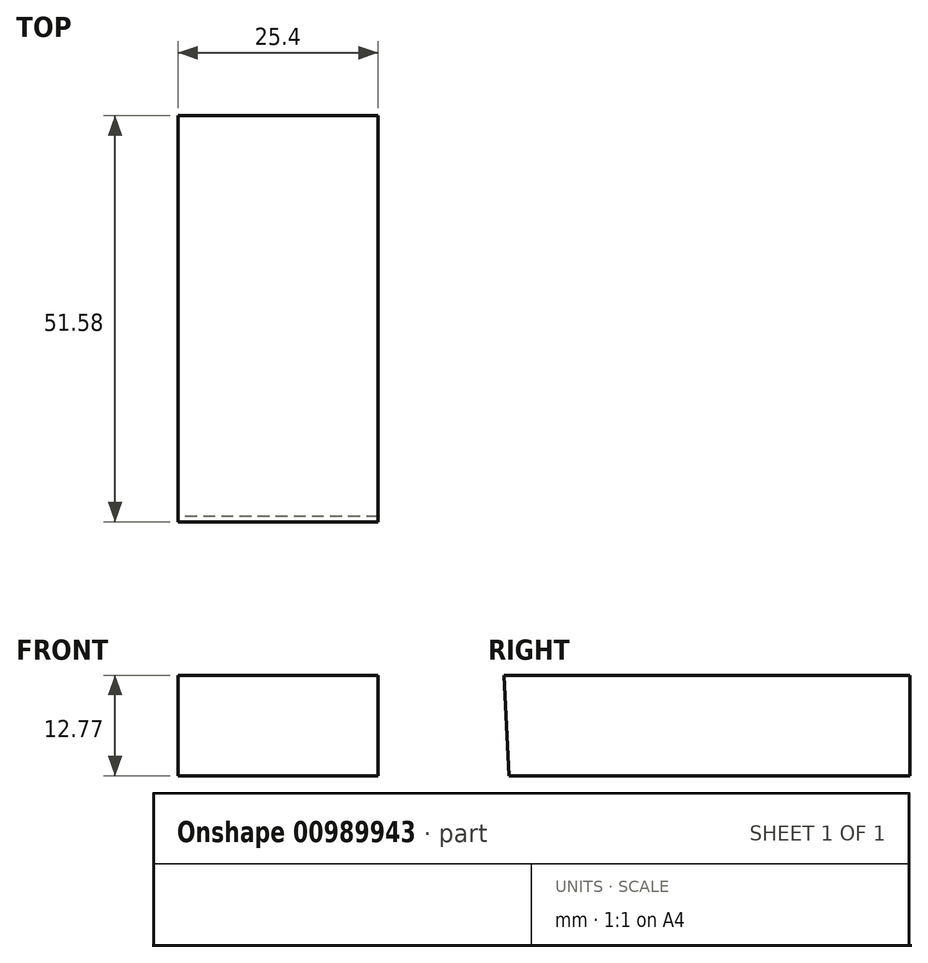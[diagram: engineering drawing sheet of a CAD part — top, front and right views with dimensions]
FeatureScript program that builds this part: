
annotation { "Feature Type Name" : "Feature", "Feature Type Description" : "" }
export const myFeature = defineFeature(function(context is Context, id is Id, definition is map)
    precondition{}
    {
        {
            var Q0;
            Q0=qCreatedBy(makeId("Right.planeOp"),FACE);
            var sketch = newSketch(context, id + "F0", { "sketchPlane" : qUnion([Q0])});
            skLineSegment(sketch, "E0", {"start": v(-72.6, 39.9) * mm, "end": v(-21.02, 39.9) * mm});
            skLineSegment(sketch, "E1", {"start": v(-21.02, 39.9) * mm, "end": v(-21.02, 27.13) * mm});
            skLineSegment(sketch, "E2", {"start": v(-21.02, 27.13) * mm, "end": v(-71.94, 27.13) * mm});
            skLineSegment(sketch, "E3", {"start": v(-71.94, 27.13) * mm, "end": v(-72.6, 39.9) * mm});
            skSolve(sketch);
        }
        {
            var Q0;
            Q0=makeQuery(id+"F0.imprint","IMPRINT",FACE,{"disambiguationData":[TD([[makeQuery(id+"F0.imprint","IMPRINT",EDGE,{"derivedFrom":sQuery(id+"F0.wireOp",EDGE,"E0")}),-1.0]])]});
            extrude(context, id + "F1", {"entities" : qUnion([Q0]), "depth" : 25.4 * mm, "offsetDistance" : 25.4 * mm});
        }
    });
